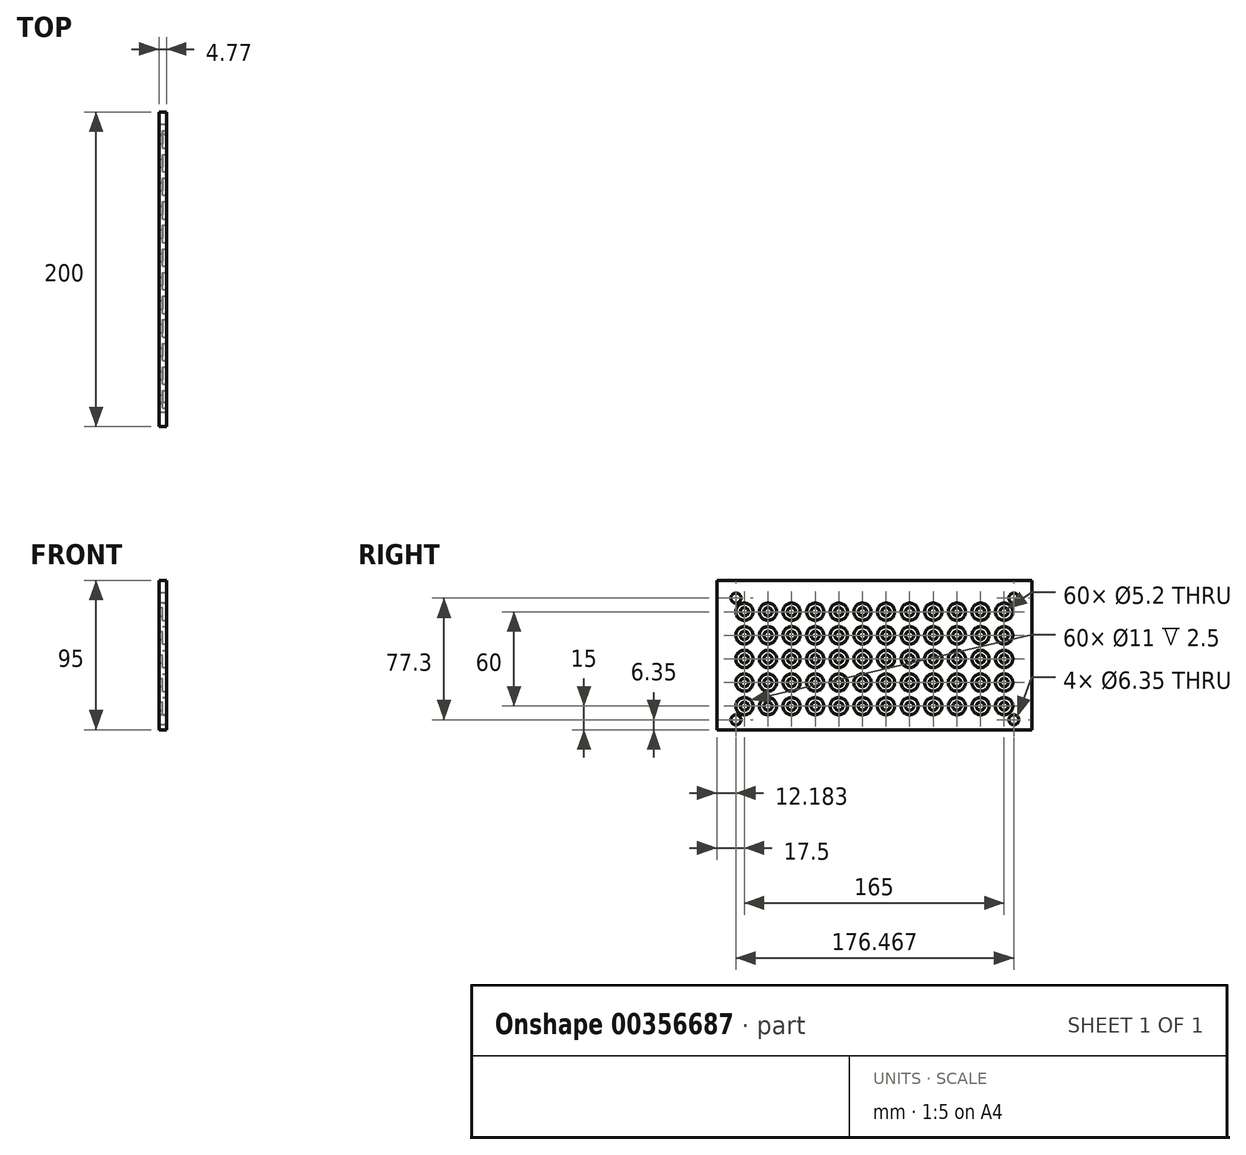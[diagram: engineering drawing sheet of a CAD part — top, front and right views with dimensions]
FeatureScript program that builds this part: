
annotation { "Feature Type Name" : "Feature", "Feature Type Description" : "" }
export const myFeature = defineFeature(function(context is Context, id is Id, definition is map)
    precondition{}
    {
        {
            var Q0;
            Q0=qCreatedBy(makeId("Right.planeOp"),FACE);
            var sketch = newSketch(context, id + "F0", { "sketchPlane" : qUnion([Q0])});
            skLineSegment(sketch, "E0.bottom", {"start": v(-100, 50) * mm, "end": v(100, 50) * mm, "construction": true});
            skLineSegment(sketch, "E0.top", {"start": v(-100, -50) * mm, "end": v(100, -50) * mm, "construction": true});
            skLineSegment(sketch, "E0.left", {"start": v(-100, 50) * mm, "end": v(-100, -45) * mm});
            skLineSegment(sketch, "E0.right", {"start": v(100, 50) * mm, "end": v(100, -45) * mm});
            skLineSegment(sketch, "E1", {"start": v(-100, -45) * mm, "end": v(100, -45) * mm});
            skCircle(sketch, "E2", {"center": v(-87.82, -38.65) * mm, "radius": 3.18 * mm});
            skCircle(sketch, "E3", {"center": v(-87.82, 38.65) * mm, "radius": 3.18 * mm});
            skCircle(sketch, "E4", {"center": v(88.65, 38.65) * mm, "radius": 3.18 * mm});
            skCircle(sketch, "E5", {"center": v(88.65, -38.65) * mm, "radius": 3.18 * mm});
            skLineSegment(sketch, "E6", {"start": v(-100, 45) * mm, "end": v(100, 45) * mm, "construction": true});
            skLineSegment(sketch, "E7", {"start": v(-95, 50) * mm, "end": v(-95, -45) * mm, "construction": true});
            skLineSegment(sketch, "E8", {"start": v(95, 50) * mm, "end": v(95, -45) * mm, "construction": true});
            skLineSegment(sketch, "E9", {"start": v(-100, 50) * mm, "end": v(100, 50) * mm});
            skSolve(sketch);
        }
        {
            var Q0;
            Q0=makeQuery(id+"F0.imprint","IMPRINT",FACE,{"disambiguationData":[TD([[makeQuery(id+"F0.imprint","IMPRINT",EDGE,{"derivedFrom":sQuery(id+"F0.wireOp",EDGE,"E0.left")}),1.0]])]});
            extrude(context, id + "F1", {"entities" : qUnion([Q0]), "depth" : 4.77 * mm});
        }
        {
            var Q0;
            Q0=makeQuery(id+"F1.opExtrude","CAP_FACE",FACE,{"disambiguationData":[OSD([sQuery(id+"F0.wireOp",EDGE,"E0.left"),sQuery(id+"F0.wireOp",EDGE,"E0.right"),sQuery(id+"F0.wireOp",EDGE,"E1"),sQuery(id+"F0.wireOp",EDGE,"E2"),sQuery(id+"F0.wireOp",EDGE,"E3"),sQuery(id+"F0.wireOp",EDGE,"E4"),sQuery(id+"F0.wireOp",EDGE,"E5"),sQuery(id+"F0.wireOp",EDGE,"E9")])],"isStart":false});
            var sketch = newSketch(context, id + "F2", { "sketchPlane" : qUnion([Q0])});
            skCircle(sketch, "E10", {"center": v(-82.5, 30) * mm, "radius": 2.6 * mm});
            skCircle(sketch, "E11.0.1.0", {"center": v(-82.5, 15) * mm, "radius": 2.6 * mm});
            skCircle(sketch, "E11.0.2.0", {"center": v(-82.5, 0) * mm, "radius": 2.6 * mm});
            skCircle(sketch, "E11.0.3.0", {"center": v(-82.5, -15) * mm, "radius": 2.6 * mm});
            skCircle(sketch, "E11.1.0.0", {"center": v(-67.5, 30) * mm, "radius": 2.6 * mm});
            skCircle(sketch, "E11.1.1.0", {"center": v(-67.5, 15) * mm, "radius": 2.6 * mm});
            skCircle(sketch, "E11.1.2.0", {"center": v(-67.5, 0) * mm, "radius": 2.6 * mm});
            skCircle(sketch, "E11.1.3.0", {"center": v(-67.5, -15) * mm, "radius": 2.6 * mm});
            skCircle(sketch, "E11.2.0.0", {"center": v(-52.5, 30) * mm, "radius": 2.6 * mm});
            skCircle(sketch, "E11.2.1.0", {"center": v(-52.5, 15) * mm, "radius": 2.6 * mm});
            skCircle(sketch, "E11.2.2.0", {"center": v(-52.5, 0) * mm, "radius": 2.6 * mm});
            skCircle(sketch, "E11.2.3.0", {"center": v(-52.5, -15) * mm, "radius": 2.6 * mm});
            skCircle(sketch, "E11.3.0.0", {"center": v(-37.5, 30) * mm, "radius": 2.6 * mm});
            skCircle(sketch, "E11.3.1.0", {"center": v(-37.5, 15) * mm, "radius": 2.6 * mm});
            skCircle(sketch, "E11.3.2.0", {"center": v(-37.5, 0) * mm, "radius": 2.6 * mm});
            skCircle(sketch, "E11.3.3.0", {"center": v(-37.5, -15) * mm, "radius": 2.6 * mm});
            skCircle(sketch, "E11.4.0.0", {"center": v(-22.5, 30) * mm, "radius": 2.6 * mm});
            skCircle(sketch, "E11.4.1.0", {"center": v(-22.5, 15) * mm, "radius": 2.6 * mm});
            skCircle(sketch, "E11.4.2.0", {"center": v(-22.5, 0) * mm, "radius": 2.6 * mm});
            skCircle(sketch, "E11.4.3.0", {"center": v(-22.5, -15) * mm, "radius": 2.6 * mm});
            skCircle(sketch, "E11.5.0.0", {"center": v(-7.5, 30) * mm, "radius": 2.6 * mm});
            skCircle(sketch, "E11.5.1.0", {"center": v(-7.5, 15) * mm, "radius": 2.6 * mm});
            skCircle(sketch, "E11.5.2.0", {"center": v(-7.5, 0) * mm, "radius": 2.6 * mm});
            skCircle(sketch, "E11.5.3.0", {"center": v(-7.5, -15) * mm, "radius": 2.6 * mm});
            skCircle(sketch, "E11.6.0.0", {"center": v(7.5, 30) * mm, "radius": 2.6 * mm});
            skCircle(sketch, "E11.6.1.0", {"center": v(7.5, 15) * mm, "radius": 2.6 * mm});
            skCircle(sketch, "E11.6.2.0", {"center": v(7.5, 0) * mm, "radius": 2.6 * mm});
            skCircle(sketch, "E11.6.3.0", {"center": v(7.5, -15) * mm, "radius": 2.6 * mm});
            skCircle(sketch, "E11.7.0.0", {"center": v(22.5, 30) * mm, "radius": 2.6 * mm});
            skCircle(sketch, "E11.7.1.0", {"center": v(22.5, 15) * mm, "radius": 2.6 * mm});
            skCircle(sketch, "E11.7.2.0", {"center": v(22.5, 0) * mm, "radius": 2.6 * mm});
            skCircle(sketch, "E11.7.3.0", {"center": v(22.5, -15) * mm, "radius": 2.6 * mm});
            skCircle(sketch, "E11.8.0.0", {"center": v(37.5, 30) * mm, "radius": 2.6 * mm});
            skCircle(sketch, "E11.8.1.0", {"center": v(37.5, 15) * mm, "radius": 2.6 * mm});
            skCircle(sketch, "E11.8.2.0", {"center": v(37.5, 0) * mm, "radius": 2.6 * mm});
            skCircle(sketch, "E11.8.3.0", {"center": v(37.5, -15) * mm, "radius": 2.6 * mm});
            skLineSegment(sketch, "E11.direction1", {"start": v(-82.5, 30) * mm, "end": v(-67.5, 30) * mm, "construction": true});
            skLineSegment(sketch, "E11.direction2", {"start": v(-82.5, 30) * mm, "end": v(-82.5, 15) * mm, "construction": true});
            skCircle(sketch, "E12.0.9.0", {"center": v(52.5, 30) * mm, "radius": 2.6 * mm});
            skCircle(sketch, "E12.0.9.1", {"center": v(52.5, 15) * mm, "radius": 2.6 * mm});
            skCircle(sketch, "E12.0.9.2", {"center": v(52.5, 0) * mm, "radius": 2.6 * mm});
            skCircle(sketch, "E12.0.9.3", {"center": v(52.5, -15) * mm, "radius": 2.6 * mm});
            skCircle(sketch, "E12.0.10.0", {"center": v(67.5, 30) * mm, "radius": 2.6 * mm});
            skCircle(sketch, "E12.0.10.1", {"center": v(67.5, 15) * mm, "radius": 2.6 * mm});
            skCircle(sketch, "E12.0.10.2", {"center": v(67.5, 0) * mm, "radius": 2.6 * mm});
            skCircle(sketch, "E12.0.10.3", {"center": v(67.5, -15) * mm, "radius": 2.6 * mm});
            skCircle(sketch, "E12.0.11.0", {"center": v(82.5, 30) * mm, "radius": 2.6 * mm});
            skCircle(sketch, "E12.0.11.1", {"center": v(82.5, 15) * mm, "radius": 2.6 * mm});
            skCircle(sketch, "E12.0.11.2", {"center": v(82.5, 0) * mm, "radius": 2.6 * mm});
            skCircle(sketch, "E12.0.11.3", {"center": v(82.5, -15) * mm, "radius": 2.6 * mm});
            skCircle(sketch, "E13.0.0.4", {"center": v(-82.5, -30) * mm, "radius": 2.6 * mm});
            skCircle(sketch, "E13.0.1.4", {"center": v(-67.5, -30) * mm, "radius": 2.6 * mm});
            skCircle(sketch, "E13.0.2.4", {"center": v(-52.5, -30) * mm, "radius": 2.6 * mm});
            skCircle(sketch, "E13.0.3.4", {"center": v(-37.5, -30) * mm, "radius": 2.6 * mm});
            skCircle(sketch, "E13.0.4.4", {"center": v(-22.5, -30) * mm, "radius": 2.6 * mm});
            skCircle(sketch, "E13.0.5.4", {"center": v(-7.5, -30) * mm, "radius": 2.6 * mm});
            skCircle(sketch, "E13.0.6.4", {"center": v(7.5, -30) * mm, "radius": 2.6 * mm});
            skCircle(sketch, "E13.0.7.4", {"center": v(22.5, -30) * mm, "radius": 2.6 * mm});
            skCircle(sketch, "E13.0.8.4", {"center": v(37.5, -30) * mm, "radius": 2.6 * mm});
            skCircle(sketch, "E13.0.9.4", {"center": v(52.5, -30) * mm, "radius": 2.6 * mm});
            skCircle(sketch, "E13.0.10.4", {"center": v(67.5, -30) * mm, "radius": 2.6 * mm});
            skCircle(sketch, "E13.0.11.4", {"center": v(82.5, -30) * mm, "radius": 2.6 * mm});
            skSolve(sketch);
        }
        {
            var Q0;
            Q0=qSketchRegion(id+"F2",true);
            extrude(context, id + "F3", {"entities" : qUnion([Q0]), "operationType" : NewBodyOperationType.REMOVE, "endBound" : BoundingType.UP_TO_NEXT, "oppositeDirection" : true, "depth" : 25 * mm});
        }
        {
            var Q0;
            Q0=makeQuery(id+"F1.opExtrude","CAP_FACE",FACE,{"disambiguationData":[OSD([sQuery(id+"F0.wireOp",EDGE,"E0.left"),sQuery(id+"F0.wireOp",EDGE,"E0.right"),sQuery(id+"F0.wireOp",EDGE,"E1"),sQuery(id+"F0.wireOp",EDGE,"E2"),sQuery(id+"F0.wireOp",EDGE,"E3"),sQuery(id+"F0.wireOp",EDGE,"E4"),sQuery(id+"F0.wireOp",EDGE,"E5"),sQuery(id+"F0.wireOp",EDGE,"E9")])],"isStart":false});
            var sketch = newSketch(context, id + "F4", { "sketchPlane" : qUnion([Q0])});
            skCircle(sketch, "E14", {"center": v(-82.5, 30) * mm, "radius": 5.5 * mm});
            skCircle(sketch, "E15.0.1.0", {"center": v(-82.5, 15) * mm, "radius": 5.5 * mm});
            skCircle(sketch, "E15.0.2.0", {"center": v(-82.5, 0) * mm, "radius": 5.5 * mm});
            skCircle(sketch, "E15.0.3.0", {"center": v(-82.5, -15) * mm, "radius": 5.5 * mm});
            skCircle(sketch, "E15.1.0.0", {"center": v(-67.5, 30) * mm, "radius": 5.5 * mm});
            skCircle(sketch, "E15.1.1.0", {"center": v(-67.5, 15) * mm, "radius": 5.5 * mm});
            skCircle(sketch, "E15.1.2.0", {"center": v(-67.5, 0) * mm, "radius": 5.5 * mm});
            skCircle(sketch, "E15.1.3.0", {"center": v(-67.5, -15) * mm, "radius": 5.5 * mm});
            skCircle(sketch, "E15.2.0.0", {"center": v(-52.5, 30) * mm, "radius": 5.5 * mm});
            skCircle(sketch, "E15.2.1.0", {"center": v(-52.5, 15) * mm, "radius": 5.5 * mm});
            skCircle(sketch, "E15.2.2.0", {"center": v(-52.5, 0) * mm, "radius": 5.5 * mm});
            skCircle(sketch, "E15.2.3.0", {"center": v(-52.5, -15) * mm, "radius": 5.5 * mm});
            skCircle(sketch, "E15.3.0.0", {"center": v(-37.5, 30) * mm, "radius": 5.5 * mm});
            skCircle(sketch, "E15.3.1.0", {"center": v(-37.5, 15) * mm, "radius": 5.5 * mm});
            skCircle(sketch, "E15.3.2.0", {"center": v(-37.5, 0) * mm, "radius": 5.5 * mm});
            skCircle(sketch, "E15.3.3.0", {"center": v(-37.5, -15) * mm, "radius": 5.5 * mm});
            skCircle(sketch, "E15.4.0.0", {"center": v(-22.5, 30) * mm, "radius": 5.5 * mm});
            skCircle(sketch, "E15.4.1.0", {"center": v(-22.5, 15) * mm, "radius": 5.5 * mm});
            skCircle(sketch, "E15.4.2.0", {"center": v(-22.5, 0) * mm, "radius": 5.5 * mm});
            skCircle(sketch, "E15.4.3.0", {"center": v(-22.5, -15) * mm, "radius": 5.5 * mm});
            skCircle(sketch, "E15.5.0.0", {"center": v(-7.5, 30) * mm, "radius": 5.5 * mm});
            skCircle(sketch, "E15.5.1.0", {"center": v(-7.5, 15) * mm, "radius": 5.5 * mm});
            skCircle(sketch, "E15.5.2.0", {"center": v(-7.5, 0) * mm, "radius": 5.5 * mm});
            skCircle(sketch, "E15.5.3.0", {"center": v(-7.5, -15) * mm, "radius": 5.5 * mm});
            skCircle(sketch, "E15.6.0.0", {"center": v(7.5, 30) * mm, "radius": 5.5 * mm});
            skCircle(sketch, "E15.6.1.0", {"center": v(7.5, 15) * mm, "radius": 5.5 * mm});
            skCircle(sketch, "E15.6.2.0", {"center": v(7.5, 0) * mm, "radius": 5.5 * mm});
            skCircle(sketch, "E15.6.3.0", {"center": v(7.5, -15) * mm, "radius": 5.5 * mm});
            skCircle(sketch, "E15.7.0.0", {"center": v(22.5, 30) * mm, "radius": 5.5 * mm});
            skCircle(sketch, "E15.7.1.0", {"center": v(22.5, 15) * mm, "radius": 5.5 * mm});
            skCircle(sketch, "E15.7.2.0", {"center": v(22.5, 0) * mm, "radius": 5.5 * mm});
            skCircle(sketch, "E15.7.3.0", {"center": v(22.5, -15) * mm, "radius": 5.5 * mm});
            skCircle(sketch, "E15.8.0.0", {"center": v(37.5, 30) * mm, "radius": 5.5 * mm});
            skCircle(sketch, "E15.8.1.0", {"center": v(37.5, 15) * mm, "radius": 5.5 * mm});
            skCircle(sketch, "E15.8.2.0", {"center": v(37.5, 0) * mm, "radius": 5.5 * mm});
            skCircle(sketch, "E15.8.3.0", {"center": v(37.5, -15) * mm, "radius": 5.5 * mm});
            skLineSegment(sketch, "E15.direction1", {"start": v(-82.5, 30) * mm, "end": v(-67.5, 30) * mm, "construction": true});
            skLineSegment(sketch, "E15.direction2", {"start": v(-82.5, 30) * mm, "end": v(-82.5, 15) * mm, "construction": true});
            skCircle(sketch, "E16.0.0.4", {"center": v(-82.5, -30) * mm, "radius": 5.5 * mm});
            skCircle(sketch, "E16.0.1.4", {"center": v(-67.5, -30) * mm, "radius": 5.5 * mm});
            skCircle(sketch, "E16.0.2.4", {"center": v(-52.5, -30) * mm, "radius": 5.5 * mm});
            skCircle(sketch, "E16.0.3.4", {"center": v(-37.5, -30) * mm, "radius": 5.5 * mm});
            skCircle(sketch, "E16.0.4.4", {"center": v(-22.5, -30) * mm, "radius": 5.5 * mm});
            skCircle(sketch, "E16.0.5.4", {"center": v(-7.5, -30) * mm, "radius": 5.5 * mm});
            skCircle(sketch, "E16.0.6.4", {"center": v(7.5, -30) * mm, "radius": 5.5 * mm});
            skCircle(sketch, "E16.0.7.4", {"center": v(22.5, -30) * mm, "radius": 5.5 * mm});
            skCircle(sketch, "E16.0.8.4", {"center": v(37.5, -30) * mm, "radius": 5.5 * mm});
            skCircle(sketch, "E17.0.9.0", {"center": v(52.5, 30) * mm, "radius": 5.5 * mm});
            skCircle(sketch, "E17.0.9.1", {"center": v(52.5, 15) * mm, "radius": 5.5 * mm});
            skCircle(sketch, "E17.0.9.2", {"center": v(52.5, 0) * mm, "radius": 5.5 * mm});
            skCircle(sketch, "E17.0.9.3", {"center": v(52.5, -15) * mm, "radius": 5.5 * mm});
            skCircle(sketch, "E17.0.9.4", {"center": v(52.5, -30) * mm, "radius": 5.5 * mm});
            skCircle(sketch, "E17.0.10.0", {"center": v(67.5, 30) * mm, "radius": 5.5 * mm});
            skCircle(sketch, "E17.0.10.1", {"center": v(67.5, 15) * mm, "radius": 5.5 * mm});
            skCircle(sketch, "E17.0.10.2", {"center": v(67.5, 0) * mm, "radius": 5.5 * mm});
            skCircle(sketch, "E17.0.10.3", {"center": v(67.5, -15) * mm, "radius": 5.5 * mm});
            skCircle(sketch, "E17.0.10.4", {"center": v(67.5, -30) * mm, "radius": 5.5 * mm});
            skCircle(sketch, "E17.0.11.0", {"center": v(82.5, 30) * mm, "radius": 5.5 * mm});
            skCircle(sketch, "E17.0.11.1", {"center": v(82.5, 15) * mm, "radius": 5.5 * mm});
            skCircle(sketch, "E17.0.11.2", {"center": v(82.5, 0) * mm, "radius": 5.5 * mm});
            skCircle(sketch, "E17.0.11.3", {"center": v(82.5, -15) * mm, "radius": 5.5 * mm});
            skCircle(sketch, "E17.0.11.4", {"center": v(82.5, -30) * mm, "radius": 5.5 * mm});
            skSolve(sketch);
        }
        {
            var Q0;
            Q0=qSketchRegion(id+"F4",true);
            extrude(context, id + "F5", {"entities" : qUnion([Q0]), "operationType" : NewBodyOperationType.REMOVE, "oppositeDirection" : true, "depth" : 2.5 * mm});
        }
    });
